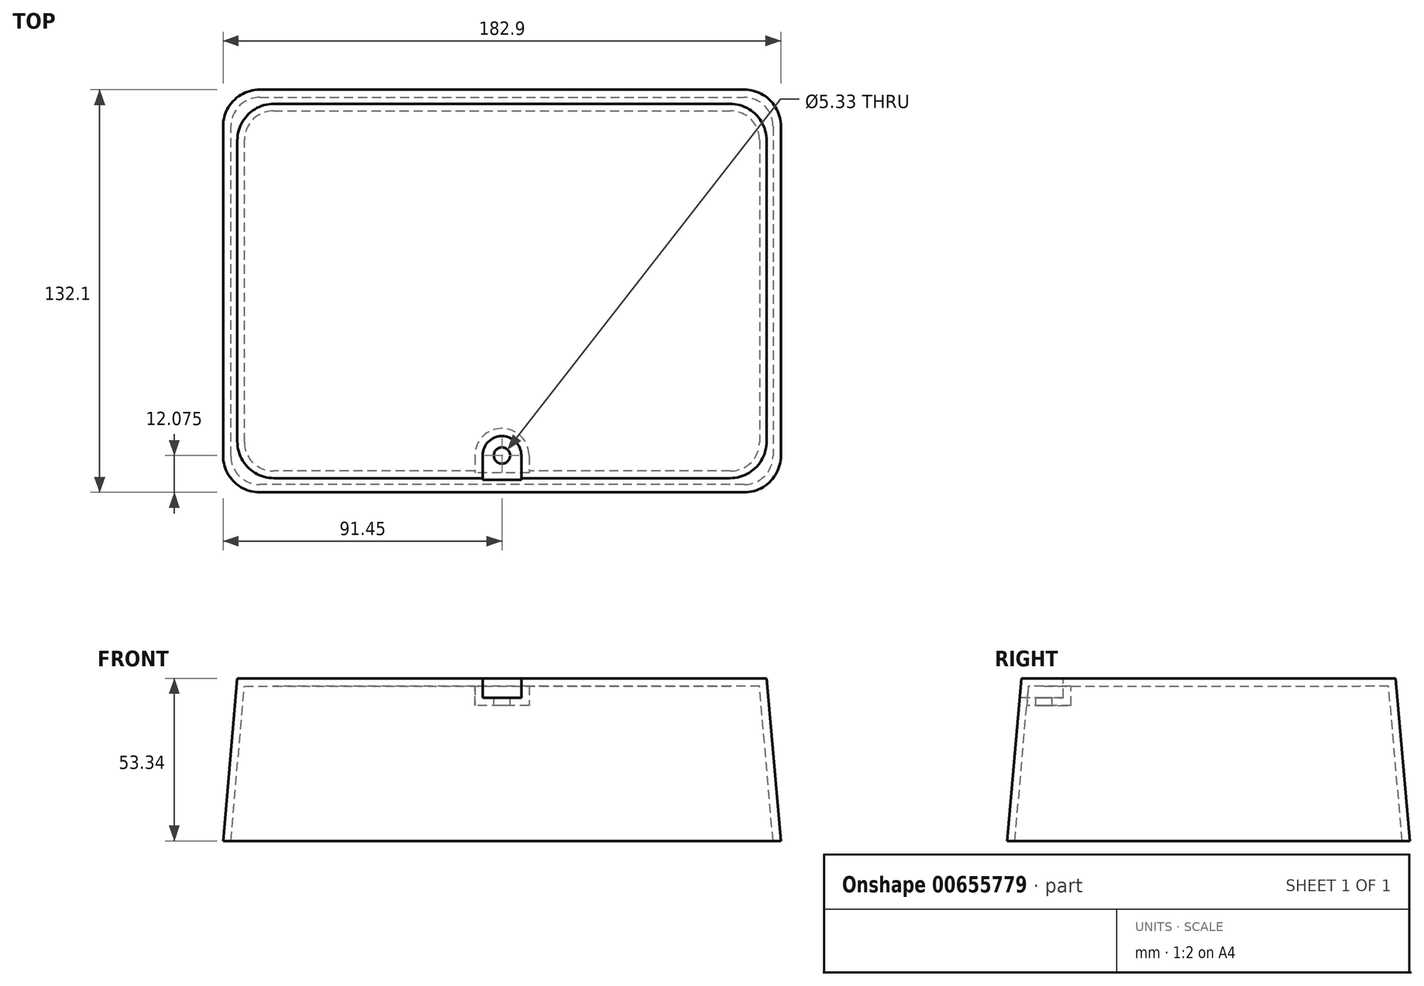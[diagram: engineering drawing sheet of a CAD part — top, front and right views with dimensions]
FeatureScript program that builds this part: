
annotation { "Feature Type Name" : "Feature", "Feature Type Description" : "" }
export const myFeature = defineFeature(function(context is Context, id is Id, definition is map)
    precondition{}
    {
        {
            var Q0;
            Q0=qCreatedBy(makeId("Top.planeOp"),FACE);
            var sketch = newSketch(context, id + "F0", { "sketchPlane" : qUnion([Q0])});
            skLineSegment(sketch, "E0.bottom", {"start": v(88.9, 63.5) * mm, "end": v(-88.9, 63.5) * mm});
            skLineSegment(sketch, "E0.top", {"start": v(88.9, -63.5) * mm, "end": v(-88.9, -63.5) * mm});
            skLineSegment(sketch, "E0.left", {"start": v(88.9, 63.5) * mm, "end": v(88.9, -63.5) * mm});
            skLineSegment(sketch, "E0.right", {"start": v(-88.9, 63.5) * mm, "end": v(-88.9, -63.5) * mm});
            skPoint(sketch, "E0.middle", {"position": v(0, 0) * mm});
            skSolve(sketch);
        }
        {
            var Q0;
            Q0 = qSketchRegion(id + "F0", true);
            extrude(context, id + "F1", {"entities" : qUnion([Q0]), "depth" : 50.8 * mm, "offsetDistance" : 25.4 * mm, "hasDraft" : true, "draftAngle" : 5 * degree, "draftPullDirection" : true});
        }
        {
            var Q0;
            Q0=makeQuery(id+"F1.opExtrude","CAP_FACE",FACE,{"disambiguationData":[OSD([sQuery(id+"F0.wireOp",EDGE,"E0.bottom"),sQuery(id+"F0.wireOp",EDGE,"E0.top"),sQuery(id+"F0.wireOp",EDGE,"E0.left"),sQuery(id+"F0.wireOp",EDGE,"E0.right")])],"isStart":false});
            var sketch = newSketch(context, id + "F2", { "sketchPlane" : qUnion([Q0])});
            skCircle(sketch, "E1", {"center": v(0, -53.98) * mm, "radius": 2.54 * mm});
            skSolve(sketch);
        }
        {
            var Q0;
            Q0=makeQuery(id+"F2.imprint","IMPRINT",FACE,{"disambiguationData":[TD([[makeQuery(id+"F2.imprint","IMPRINT",EDGE,{"derivedFrom":sQuery(id+"F2.wireOp",EDGE,"E1")}),-1.0]])]});
            var sketch = newSketch(context, id + "F3", { "sketchPlane" : qUnion([Q0])});
            skLineSegment(sketch, "E2", {"start": v(0, -53.98) * mm, "end": v(0.02, -67.85) * mm});
            skArc(sketch, "E3.0.startCap", {"start": v(-8.89, -53.99) * mm, "mid": v(-0.01, -45.09) * mm, "end": v(8.89, -53.96) * mm});
            skArc(sketch, "E3.0.endCap", {"start": v(8.91, -67.84) * mm, "mid": v(0.04, -76.74) * mm, "end": v(-8.87, -67.87) * mm});
            skLineSegment(sketch, "E3.0.left", {"start": v(8.89, -53.96) * mm, "end": v(8.91, -67.84) * mm});
            skLineSegment(sketch, "E3.0.right", {"start": v(-8.89, -53.99) * mm, "end": v(-8.87, -67.87) * mm});
            skSolve(sketch);
        }
        {
            var Q0;
            Q0 = qSketchRegion(id + "F3", true);
            extrude(context, id + "F4", {"entities" : qUnion([Q0]), "operationType" : NewBodyOperationType.REMOVE, "oppositeDirection" : true, "depth" : 6.35 * mm, "offsetDistance" : 25.4 * mm});
        }
        {
            var Q0;
            Q0=makeQuery(id+"F1.opExtrude","SWEPT_EDGE",EDGE,{"disambiguationData":[OSD([sQuery(id+"F0.wireOp",EDGE,"E0.bottom"),sQuery(id+"F0.wireOp",EDGE,"E0.right")])]});
            var Q1;
            Q1=makeQuery(id+"F1.opExtrude","SWEPT_EDGE",EDGE,{"disambiguationData":[OSD([sQuery(id+"F0.wireOp",EDGE,"E0.top"),sQuery(id+"F0.wireOp",EDGE,"E0.right")])]});
            var Q2;
            Q2=makeQuery(id+"F1.opExtrude","SWEPT_EDGE",EDGE,{"disambiguationData":[OSD([sQuery(id+"F0.wireOp",EDGE,"E0.bottom"),sQuery(id+"F0.wireOp",EDGE,"E0.left")])]});
            var Q3;
            Q3=makeQuery(id+"F1.opExtrude","SWEPT_EDGE",EDGE,{"disambiguationData":[OSD([sQuery(id+"F0.wireOp",EDGE,"E0.top"),sQuery(id+"F0.wireOp",EDGE,"E0.left")])]});
            fillet(context, id + "F5", {"entities" : qUnion([Q0, Q1, Q2, Q3]), "radius" : 9.52 * mm, "tangentPropagation" : true, "allowEdgeOverflow" : false});
        }
        {
            var Q0;
            Q0=makeQuery(id+"F1.opExtrude","CAP_FACE",FACE,{"disambiguationData":[OSD([sQuery(id+"F0.wireOp",EDGE,"E0.bottom"),sQuery(id+"F0.wireOp",EDGE,"E0.top"),sQuery(id+"F0.wireOp",EDGE,"E0.left"),sQuery(id+"F0.wireOp",EDGE,"E0.right")])],"isStart":true});
            shell(context, id + "F6", {"entities" : qUnion([Q0]), "thickness" : 2.54 * mm, "oppositeDirection" : true});
        }
        {
            var Q0;
            Q0=sQuery(id+"F2.wireOp",VERTEX,"E1.center");
            var Q1;
            Q1=makeQuery(id+"F1.opExtrude","SWEPT_BODY",BODY,{"disambiguationData":[OSD([sQuery(id+"F0.wireOp",EDGE,"E0.bottom"),sQuery(id+"F0.wireOp",EDGE,"E0.top"),sQuery(id+"F0.wireOp",EDGE,"E0.left"),sQuery(id+"F0.wireOp",EDGE,"E0.right")])]});
            hole(context, id + "F7", {"style" : HoleStyle.SIMPLE, "endStyle" : HoleEndStyle.THROUGH, "holeDiameter" : 5.33 * mm, "majorDiameter" : 6.35 * mm, "isTappedThrough" : true, "tappedDepth" : 12.7 * mm, "tapClearance" : 3, "locations" : qUnion([Q0]), "scope" : qUnion([Q1])});
        }
    });
